# Revit family: Artek_Lighting_Pendant Light A110 “Hand Grenade”_A110 “Hand Grenade“_quick_ship
name_source: partatom
category: Lighting Fixtures
revit_build: Autodesk Revit 2018 (Build: 20170223_1515(x64)
units: mm (PartAtom-declared; Revit-internal decimal feet)

## family parameters
Always vertical = Yes
Cut with Voids When Loaded = No
Light Source = Yes
OmniClass Number = 23.80.70.00
OmniClass Title = Lighting
Part Type = Normal
Room Calculation Point = No
Round Connector Dimension = Use Diameter
Shared = No
Work Plane-Based = No

## types (4) — shared parameters
AssetType = Fixed
BIMObjectName = Artek_Lighting_Pendant Light A110 “Hand Grenade”_A110 “Hand Grenade“_quick_ship
Brand = Artek
Category = Lighting
Collection = Pendant Lights
Color Filter = 16777215
ConvergoRefNr = 0190-2009-0053-FI
Description = This elegant pendant light is nicknamed “Hand Grenade” for its distinctive shape.
Designer = Alvar Aalto
Dimming Lamp Color Temperature Shift = <None>
DurationUnit = Years
HasProtectiveEarth = No
IP_Code = IP20
IfcExportAs = IfcLightFixtureType
IfcExportType = NOTDEFINED
InsulationStandardClass = Class II
Light Source Symbol Size = 610 mm
LightFixtureMountingType = Suspended
LightFixturePlacingType = Ceiling
Manufacturer = Artek
ManufacturerName = Artek
ManufacturerURL = https://www.artek.fi
ManufacturersSpecificInformation = This luminaire is compatible with bulbs of the energy classes: A to G
Material = Steel, powder coated
NBSDescription = General purpose luminaires
NBSReference = 90-60-50/405
NominalCurrent = 0 A
NominalDiameter = 150 mm
NominalFrequencyRange = 60 Hz
NominalLength = 150 mm
NominalRadius = 75 mm  [stored 0.246063 ft]
NominalVoltage = 240 V
NominalVoltageCalc = 0 V
NominalWidth = 150 mm
NumberOfPoles = 1
PhaseAngle = 0.00°
ProductInformation = This elegant pendant light is nicknamed “Hand Grenade” for its distinctive shape.
Shape = Sculptured
Size = 160x440x160 mm
Socket = E27
TotalWattage = 12 W
URL = https://www.artek.fi
Uniclass2 = Pr_70_70_49_86
Uniclass2015Description = Pendant  luminaires
Uniclass2015Reference = Pr_70_70_48_62
UsageCurrent = 0 A
Version = 1
VersionDate = 11/3/2020
WarrantyDurationUnit = Years
zero-valued in all types: DefaultElevation, ElectricalDeviceNominalPower, MaintenanceFactor, NumberOfSources

## per-type parameters (varying)
| type | ArticleNumber | Color | LightFixtureMainMaterial | LightFixtureSecondaryMaterial | LightFixtureTertiaryMaterial | ModelNumber | Name |
| A110 "Hand Grenade", 29100101 | 29100101 | Black oak | Black Steel | Brass | Black plastic | 29100101 | A110 "Hand Grenade" |
| A110 "Hand Grenade", 29100102 | 29100102 | White | White Steel | Brass | White plastic | 29100102 | A110 "Hand Grenade" |
| A110 "Hand Grenade", 29100103 | 29100103 | Black | Black Steel | Black laquered | Black plastic | 29100103 | A110 “Hand Grenade“ |
| A110 "Hand Grenade", 29100104 | 29100104 | White | White Steel | White Steel | White plastic | 29100104 | A110 "Hand Grenade" |

note: column(s) folded — value = type name in every type: Model

note: [stored X ft] marks values corroborated as IEEE doubles in the binary element streams (Revit-internal decimal feet)

## geometry (parser evidence)
native form markers: Sweep x6
no freeform markers — native parametric forms only
